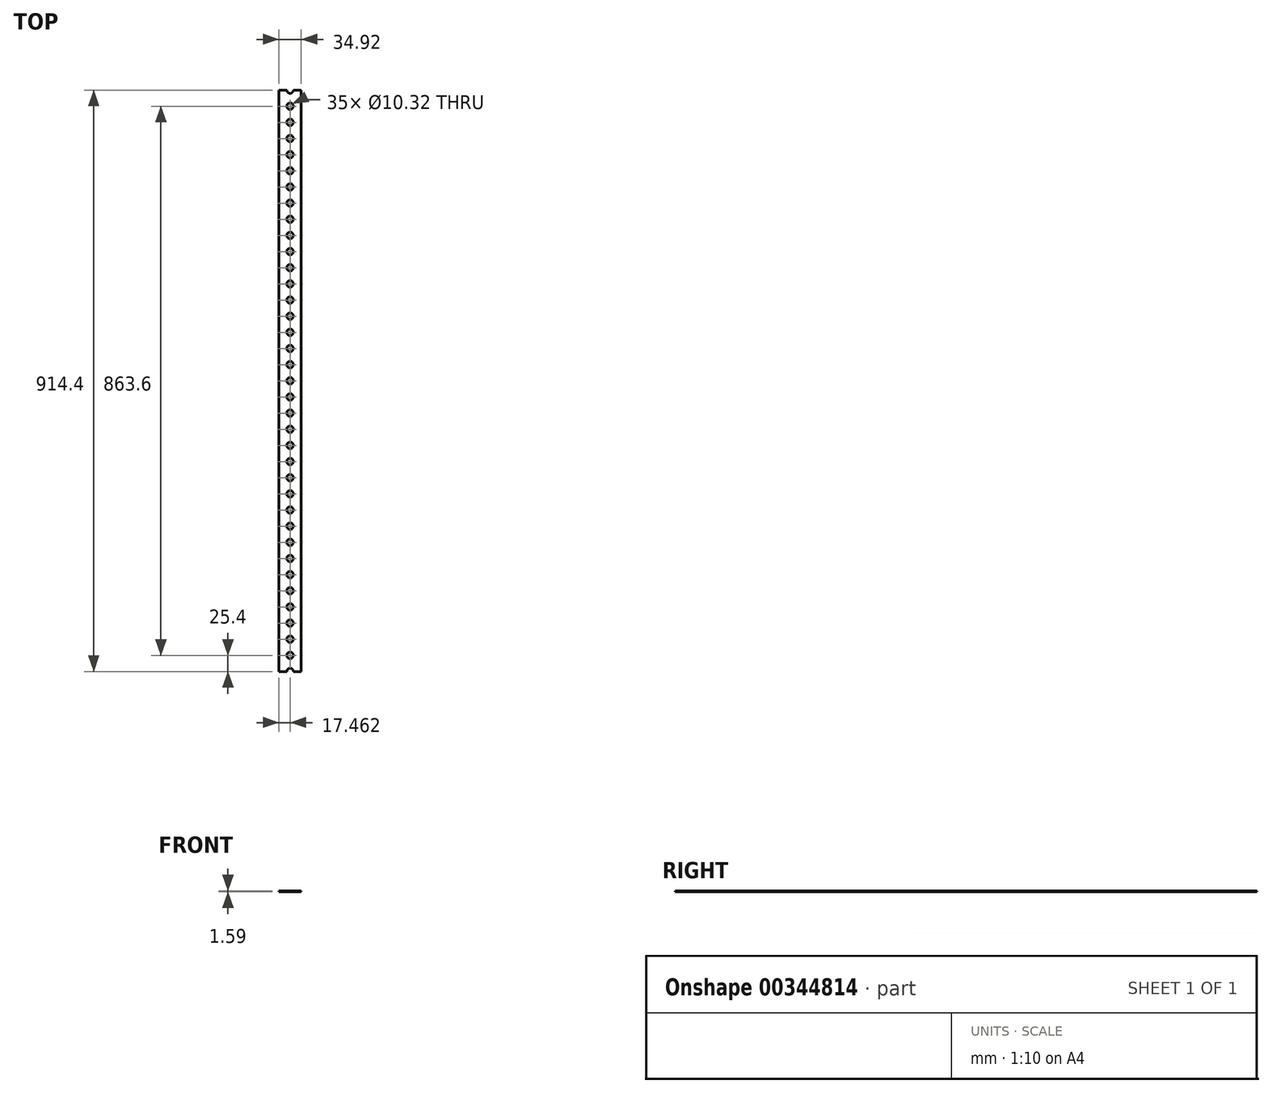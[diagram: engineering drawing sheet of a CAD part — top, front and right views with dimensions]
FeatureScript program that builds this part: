
annotation { "Feature Type Name" : "Feature", "Feature Type Description" : "" }
export const myFeature = defineFeature(function(context is Context, id is Id, definition is map)
    precondition{}
    {
        {
            var Q0;
            Q0=qCreatedBy(makeId("Front.planeOp"),FACE);
            var sketch = newSketch(context, id + "F0", { "sketchPlane" : qUnion([Q0])});
            skLineSegment(sketch, "E0.bottom", {"start": v(0, 0) * mm, "end": v(34.93, 0) * mm});
            skLineSegment(sketch, "E0.top", {"start": v(0, 1.59) * mm, "end": v(34.93, 1.59) * mm});
            skLineSegment(sketch, "E0.left", {"start": v(0, 0) * mm, "end": v(0, 1.59) * mm});
            skLineSegment(sketch, "E0.right", {"start": v(34.93, 0) * mm, "end": v(34.93, 1.59) * mm});
            skSolve(sketch);
        }
        {
            var Q0;
            Q0=makeQuery(id+"F0.imprint","IMPRINT",FACE,{"disambiguationData":[TD([[makeQuery(id+"F0.imprint","IMPRINT",EDGE,{"derivedFrom":sQuery(id+"F0.wireOp",EDGE,"E0.bottom")}),1.0]])]});
            extrude(context, id + "F1", {"entities" : qUnion([Q0]), "depth" : 914.4 * mm});
        }
        {
            var Q0;
            Q0=makeQuery(id+"F1.opExtrude","SWEPT_FACE",FACE,{"disambiguationData":[OSD([sQuery(id+"F0.wireOp",EDGE,"E0.top")])]});
            var sketch = newSketch(context, id + "F2", { "sketchPlane" : qUnion([Q0])});
            skCircle(sketch, "E1", {"center": v(17.46, -914.4) * mm, "radius": 5.16 * mm});
            skCircle(sketch, "E2.0.1.0", {"center": v(17.46, -889) * mm, "radius": 5.16 * mm});
            skCircle(sketch, "E2.0.2.0", {"center": v(17.46, -863.6) * mm, "radius": 5.16 * mm});
            skCircle(sketch, "E2.0.3.0", {"center": v(17.46, -838.2) * mm, "radius": 5.16 * mm});
            skCircle(sketch, "E2.0.4.0", {"center": v(17.46, -812.8) * mm, "radius": 5.16 * mm});
            skCircle(sketch, "E2.0.5.0", {"center": v(17.46, -787.4) * mm, "radius": 5.16 * mm});
            skCircle(sketch, "E2.0.6.0", {"center": v(17.46, -762) * mm, "radius": 5.16 * mm});
            skCircle(sketch, "E2.0.7.0", {"center": v(17.46, -736.6) * mm, "radius": 5.16 * mm});
            skCircle(sketch, "E2.0.8.0", {"center": v(17.46, -711.2) * mm, "radius": 5.16 * mm});
            skCircle(sketch, "E2.0.9.0", {"center": v(17.46, -685.8) * mm, "radius": 5.16 * mm});
            skCircle(sketch, "E2.0.10.0", {"center": v(17.46, -660.4) * mm, "radius": 5.16 * mm});
            skCircle(sketch, "E2.0.11.0", {"center": v(17.46, -635) * mm, "radius": 5.16 * mm});
            skCircle(sketch, "E2.0.12.0", {"center": v(17.46, -609.6) * mm, "radius": 5.16 * mm});
            skCircle(sketch, "E2.0.13.0", {"center": v(17.46, -584.2) * mm, "radius": 5.16 * mm});
            skCircle(sketch, "E2.0.14.0", {"center": v(17.46, -558.8) * mm, "radius": 5.16 * mm});
            skCircle(sketch, "E2.0.15.0", {"center": v(17.46, -533.4) * mm, "radius": 5.16 * mm});
            skCircle(sketch, "E2.0.16.0", {"center": v(17.46, -508) * mm, "radius": 5.16 * mm});
            skCircle(sketch, "E2.0.17.0", {"center": v(17.46, -482.6) * mm, "radius": 5.16 * mm});
            skCircle(sketch, "E2.0.18.0", {"center": v(17.46, -457.2) * mm, "radius": 5.16 * mm});
            skCircle(sketch, "E2.0.19.0", {"center": v(17.46, -431.8) * mm, "radius": 5.16 * mm});
            skCircle(sketch, "E2.0.20.0", {"center": v(17.46, -406.4) * mm, "radius": 5.16 * mm});
            skCircle(sketch, "E2.0.21.0", {"center": v(17.46, -381) * mm, "radius": 5.16 * mm});
            skCircle(sketch, "E2.0.22.0", {"center": v(17.46, -355.6) * mm, "radius": 5.16 * mm});
            skCircle(sketch, "E2.0.23.0", {"center": v(17.46, -330.2) * mm, "radius": 5.16 * mm});
            skCircle(sketch, "E2.0.24.0", {"center": v(17.46, -304.8) * mm, "radius": 5.16 * mm});
            skCircle(sketch, "E2.0.25.0", {"center": v(17.46, -279.4) * mm, "radius": 5.16 * mm});
            skCircle(sketch, "E2.0.26.0", {"center": v(17.46, -254) * mm, "radius": 5.16 * mm});
            skCircle(sketch, "E2.0.27.0", {"center": v(17.46, -228.6) * mm, "radius": 5.16 * mm});
            skCircle(sketch, "E2.0.28.0", {"center": v(17.46, -203.2) * mm, "radius": 5.16 * mm});
            skCircle(sketch, "E2.0.29.0", {"center": v(17.46, -177.8) * mm, "radius": 5.16 * mm});
            skLineSegment(sketch, "E2.direction1", {"start": v(17.46, -914.4) * mm, "end": v(42.86, -914.4) * mm, "construction": true});
            skLineSegment(sketch, "E2.direction2", {"start": v(17.46, -914.4) * mm, "end": v(17.46, -889) * mm, "construction": true});
            skCircle(sketch, "E3.0.0.30", {"center": v(17.46, -152.4) * mm, "radius": 5.16 * mm});
            skCircle(sketch, "E3.0.0.31", {"center": v(17.46, -127) * mm, "radius": 5.16 * mm});
            skCircle(sketch, "E3.0.0.32", {"center": v(17.46, -101.6) * mm, "radius": 5.16 * mm});
            skCircle(sketch, "E3.0.0.33", {"center": v(17.46, -76.2) * mm, "radius": 5.16 * mm});
            skCircle(sketch, "E3.0.0.34", {"center": v(17.46, -50.8) * mm, "radius": 5.16 * mm});
            skCircle(sketch, "E3.0.0.35", {"center": v(17.46, -25.4) * mm, "radius": 5.16 * mm});
            skCircle(sketch, "E4.0.0.36", {"center": v(17.46, 0) * mm, "radius": 5.16 * mm});
            skSolve(sketch);
        }
        {
            var Q0;
            {var subQ0=sQuery(id+"F2.wireOp",EDGE,"E4.0.0.36");var subQ1=makeQuery(id+"F1.opExtrude","CAP_EDGE",EDGE,{"disambiguationData":[OSD([sQuery(id+"F0.wireOp",EDGE,"E0.top")])],"isStart":true});var subQ2=makeQuery(id+"F2.imprint","INTERSECT",VERTEX,{"disambiguationData":[OD(0.0)],"derivedFrom":[subQ1,subQ0]});Q0=makeQuery(id+"F2.imprint","IMPRINT",FACE,{"disambiguationData":[TD([[makeQuery(id+"F2.imprint","IMPRINT",EDGE,{"disambiguationData":[TD([[subQ2,-1.0]])],"derivedFrom":subQ0}),1.0]])]});}
            var Q1;
            Q1=makeQuery(id+"F2.imprint","IMPRINT",FACE,{"disambiguationData":[TD([[makeQuery(id+"F2.imprint","IMPRINT",EDGE,{"derivedFrom":sQuery(id+"F2.wireOp",EDGE,"E3.0.0.35")}),1.0]])]});
            var Q2;
            Q2=makeQuery(id+"F2.imprint","IMPRINT",FACE,{"disambiguationData":[TD([[makeQuery(id+"F2.imprint","IMPRINT",EDGE,{"derivedFrom":sQuery(id+"F2.wireOp",EDGE,"E3.0.0.34")}),1.0]])]});
            var Q3;
            Q3=makeQuery(id+"F2.imprint","IMPRINT",FACE,{"disambiguationData":[TD([[makeQuery(id+"F2.imprint","IMPRINT",EDGE,{"derivedFrom":sQuery(id+"F2.wireOp",EDGE,"E3.0.0.32")}),1.0]])]});
            var Q4;
            Q4=makeQuery(id+"F2.imprint","IMPRINT",FACE,{"disambiguationData":[TD([[makeQuery(id+"F2.imprint","IMPRINT",EDGE,{"derivedFrom":sQuery(id+"F2.wireOp",EDGE,"E3.0.0.33")}),1.0]])]});
            var Q5;
            Q5=makeQuery(id+"F2.imprint","IMPRINT",FACE,{"disambiguationData":[TD([[makeQuery(id+"F2.imprint","IMPRINT",EDGE,{"derivedFrom":sQuery(id+"F2.wireOp",EDGE,"E2.0.27.0")}),1.0]])]});
            var Q6;
            Q6=makeQuery(id+"F2.imprint","IMPRINT",FACE,{"disambiguationData":[TD([[makeQuery(id+"F2.imprint","IMPRINT",EDGE,{"derivedFrom":sQuery(id+"F2.wireOp",EDGE,"E2.0.28.0")}),1.0]])]});
            var Q7;
            Q7=makeQuery(id+"F2.imprint","IMPRINT",FACE,{"disambiguationData":[TD([[makeQuery(id+"F2.imprint","IMPRINT",EDGE,{"derivedFrom":sQuery(id+"F2.wireOp",EDGE,"E2.0.29.0")}),1.0]])]});
            var Q8;
            Q8=makeQuery(id+"F2.imprint","IMPRINT",FACE,{"disambiguationData":[TD([[makeQuery(id+"F2.imprint","IMPRINT",EDGE,{"derivedFrom":sQuery(id+"F2.wireOp",EDGE,"E3.0.0.30")}),1.0]])]});
            var Q9;
            Q9=makeQuery(id+"F2.imprint","IMPRINT",FACE,{"disambiguationData":[TD([[makeQuery(id+"F2.imprint","IMPRINT",EDGE,{"derivedFrom":sQuery(id+"F2.wireOp",EDGE,"E3.0.0.31")}),1.0]])]});
            var Q10;
            Q10=makeQuery(id+"F2.imprint","IMPRINT",FACE,{"disambiguationData":[TD([[makeQuery(id+"F2.imprint","IMPRINT",EDGE,{"derivedFrom":sQuery(id+"F2.wireOp",EDGE,"E2.0.26.0")}),1.0]])]});
            var Q11;
            Q11=makeQuery(id+"F2.imprint","IMPRINT",FACE,{"disambiguationData":[TD([[makeQuery(id+"F2.imprint","IMPRINT",EDGE,{"derivedFrom":sQuery(id+"F2.wireOp",EDGE,"E2.0.25.0")}),1.0]])]});
            var Q12;
            Q12=makeQuery(id+"F2.imprint","IMPRINT",FACE,{"disambiguationData":[TD([[makeQuery(id+"F2.imprint","IMPRINT",EDGE,{"derivedFrom":sQuery(id+"F2.wireOp",EDGE,"E2.0.24.0")}),1.0]])]});
            var Q13;
            {var subQ0=sQuery(id+"F2.wireOp",EDGE,"E1");var subQ1=makeQuery(id+"F1.opExtrude","CAP_EDGE",EDGE,{"disambiguationData":[OSD([sQuery(id+"F0.wireOp",EDGE,"E0.top")])],"isStart":false});var subQ2=makeQuery(id+"F2.imprint","INTERSECT",VERTEX,{"disambiguationData":[OD(0.0)],"derivedFrom":[subQ1,subQ0]});Q13=makeQuery(id+"F2.imprint","IMPRINT",FACE,{"disambiguationData":[TD([[makeQuery(id+"F2.imprint","IMPRINT",EDGE,{"disambiguationData":[TD([[subQ2,1.0]])],"derivedFrom":subQ0}),1.0]])]});}
            var Q14;
            Q14=makeQuery(id+"F2.imprint","IMPRINT",FACE,{"disambiguationData":[TD([[makeQuery(id+"F2.imprint","IMPRINT",EDGE,{"derivedFrom":sQuery(id+"F2.wireOp",EDGE,"E2.0.1.0")}),1.0]])]});
            var Q15;
            Q15=makeQuery(id+"F2.imprint","IMPRINT",FACE,{"disambiguationData":[TD([[makeQuery(id+"F2.imprint","IMPRINT",EDGE,{"derivedFrom":sQuery(id+"F2.wireOp",EDGE,"E2.0.2.0")}),1.0]])]});
            var Q16;
            Q16=makeQuery(id+"F2.imprint","IMPRINT",FACE,{"disambiguationData":[TD([[makeQuery(id+"F2.imprint","IMPRINT",EDGE,{"derivedFrom":sQuery(id+"F2.wireOp",EDGE,"E2.0.3.0")}),1.0]])]});
            var Q17;
            Q17=makeQuery(id+"F2.imprint","IMPRINT",FACE,{"disambiguationData":[TD([[makeQuery(id+"F2.imprint","IMPRINT",EDGE,{"derivedFrom":sQuery(id+"F2.wireOp",EDGE,"E2.0.4.0")}),1.0]])]});
            var Q18;
            Q18=makeQuery(id+"F2.imprint","IMPRINT",FACE,{"disambiguationData":[TD([[makeQuery(id+"F2.imprint","IMPRINT",EDGE,{"derivedFrom":sQuery(id+"F2.wireOp",EDGE,"E2.0.5.0")}),1.0]])]});
            var Q19;
            Q19=makeQuery(id+"F2.imprint","IMPRINT",FACE,{"disambiguationData":[TD([[makeQuery(id+"F2.imprint","IMPRINT",EDGE,{"derivedFrom":sQuery(id+"F2.wireOp",EDGE,"E2.0.6.0")}),1.0]])]});
            var Q20;
            Q20=makeQuery(id+"F2.imprint","IMPRINT",FACE,{"disambiguationData":[TD([[makeQuery(id+"F2.imprint","IMPRINT",EDGE,{"derivedFrom":sQuery(id+"F2.wireOp",EDGE,"E2.0.7.0")}),1.0]])]});
            var Q21;
            Q21=makeQuery(id+"F2.imprint","IMPRINT",FACE,{"disambiguationData":[TD([[makeQuery(id+"F2.imprint","IMPRINT",EDGE,{"derivedFrom":sQuery(id+"F2.wireOp",EDGE,"E2.0.8.0")}),1.0]])]});
            var Q22;
            Q22=makeQuery(id+"F2.imprint","IMPRINT",FACE,{"disambiguationData":[TD([[makeQuery(id+"F2.imprint","IMPRINT",EDGE,{"derivedFrom":sQuery(id+"F2.wireOp",EDGE,"E2.0.10.0")}),1.0]])]});
            var Q23;
            Q23=makeQuery(id+"F2.imprint","IMPRINT",FACE,{"disambiguationData":[TD([[makeQuery(id+"F2.imprint","IMPRINT",EDGE,{"derivedFrom":sQuery(id+"F2.wireOp",EDGE,"E2.0.9.0")}),1.0]])]});
            var Q24;
            Q24=makeQuery(id+"F2.imprint","IMPRINT",FACE,{"disambiguationData":[TD([[makeQuery(id+"F2.imprint","IMPRINT",EDGE,{"derivedFrom":sQuery(id+"F2.wireOp",EDGE,"E2.0.11.0")}),1.0]])]});
            var Q25;
            Q25=makeQuery(id+"F2.imprint","IMPRINT",FACE,{"disambiguationData":[TD([[makeQuery(id+"F2.imprint","IMPRINT",EDGE,{"derivedFrom":sQuery(id+"F2.wireOp",EDGE,"E2.0.12.0")}),1.0]])]});
            var Q26;
            Q26=makeQuery(id+"F2.imprint","IMPRINT",FACE,{"disambiguationData":[TD([[makeQuery(id+"F2.imprint","IMPRINT",EDGE,{"derivedFrom":sQuery(id+"F2.wireOp",EDGE,"E2.0.13.0")}),1.0]])]});
            var Q27;
            Q27=makeQuery(id+"F2.imprint","IMPRINT",FACE,{"disambiguationData":[TD([[makeQuery(id+"F2.imprint","IMPRINT",EDGE,{"derivedFrom":sQuery(id+"F2.wireOp",EDGE,"E2.0.14.0")}),1.0]])]});
            var Q28;
            Q28=makeQuery(id+"F2.imprint","IMPRINT",FACE,{"disambiguationData":[TD([[makeQuery(id+"F2.imprint","IMPRINT",EDGE,{"derivedFrom":sQuery(id+"F2.wireOp",EDGE,"E2.0.15.0")}),1.0]])]});
            var Q29;
            Q29=makeQuery(id+"F2.imprint","IMPRINT",FACE,{"disambiguationData":[TD([[makeQuery(id+"F2.imprint","IMPRINT",EDGE,{"derivedFrom":sQuery(id+"F2.wireOp",EDGE,"E2.0.16.0")}),1.0]])]});
            var Q30;
            Q30=makeQuery(id+"F2.imprint","IMPRINT",FACE,{"disambiguationData":[TD([[makeQuery(id+"F2.imprint","IMPRINT",EDGE,{"derivedFrom":sQuery(id+"F2.wireOp",EDGE,"E2.0.17.0")}),1.0]])]});
            var Q31;
            Q31=makeQuery(id+"F2.imprint","IMPRINT",FACE,{"disambiguationData":[TD([[makeQuery(id+"F2.imprint","IMPRINT",EDGE,{"derivedFrom":sQuery(id+"F2.wireOp",EDGE,"E2.0.18.0")}),1.0]])]});
            var Q32;
            Q32=makeQuery(id+"F2.imprint","IMPRINT",FACE,{"disambiguationData":[TD([[makeQuery(id+"F2.imprint","IMPRINT",EDGE,{"derivedFrom":sQuery(id+"F2.wireOp",EDGE,"E2.0.19.0")}),1.0]])]});
            var Q33;
            Q33=makeQuery(id+"F2.imprint","IMPRINT",FACE,{"disambiguationData":[TD([[makeQuery(id+"F2.imprint","IMPRINT",EDGE,{"derivedFrom":sQuery(id+"F2.wireOp",EDGE,"E2.0.20.0")}),1.0]])]});
            var Q34;
            Q34=makeQuery(id+"F2.imprint","IMPRINT",FACE,{"disambiguationData":[TD([[makeQuery(id+"F2.imprint","IMPRINT",EDGE,{"derivedFrom":sQuery(id+"F2.wireOp",EDGE,"E2.0.21.0")}),1.0]])]});
            var Q35;
            Q35=makeQuery(id+"F2.imprint","IMPRINT",FACE,{"disambiguationData":[TD([[makeQuery(id+"F2.imprint","IMPRINT",EDGE,{"derivedFrom":sQuery(id+"F2.wireOp",EDGE,"E2.0.23.0")}),1.0]])]});
            var Q36;
            Q36=makeQuery(id+"F2.imprint","IMPRINT",FACE,{"disambiguationData":[TD([[makeQuery(id+"F2.imprint","IMPRINT",EDGE,{"derivedFrom":sQuery(id+"F2.wireOp",EDGE,"E2.0.22.0")}),1.0]])]});
            extrude(context, id + "F3", {"entities" : qUnion([Q0, Q1, Q2, Q3, Q4, Q5, Q6, Q7, Q8, Q9, Q10, Q11, Q12, Q13, Q14, Q15, Q16, Q17, Q18, Q19, Q20, Q21, Q22, Q23, Q24, Q25, Q26, Q27, Q28, Q29, Q30, Q31, Q32, Q33, Q34, Q35, Q36]), "operationType" : NewBodyOperationType.REMOVE, "oppositeDirection" : true, "depth" : 25.4 * mm});
        }
    });
